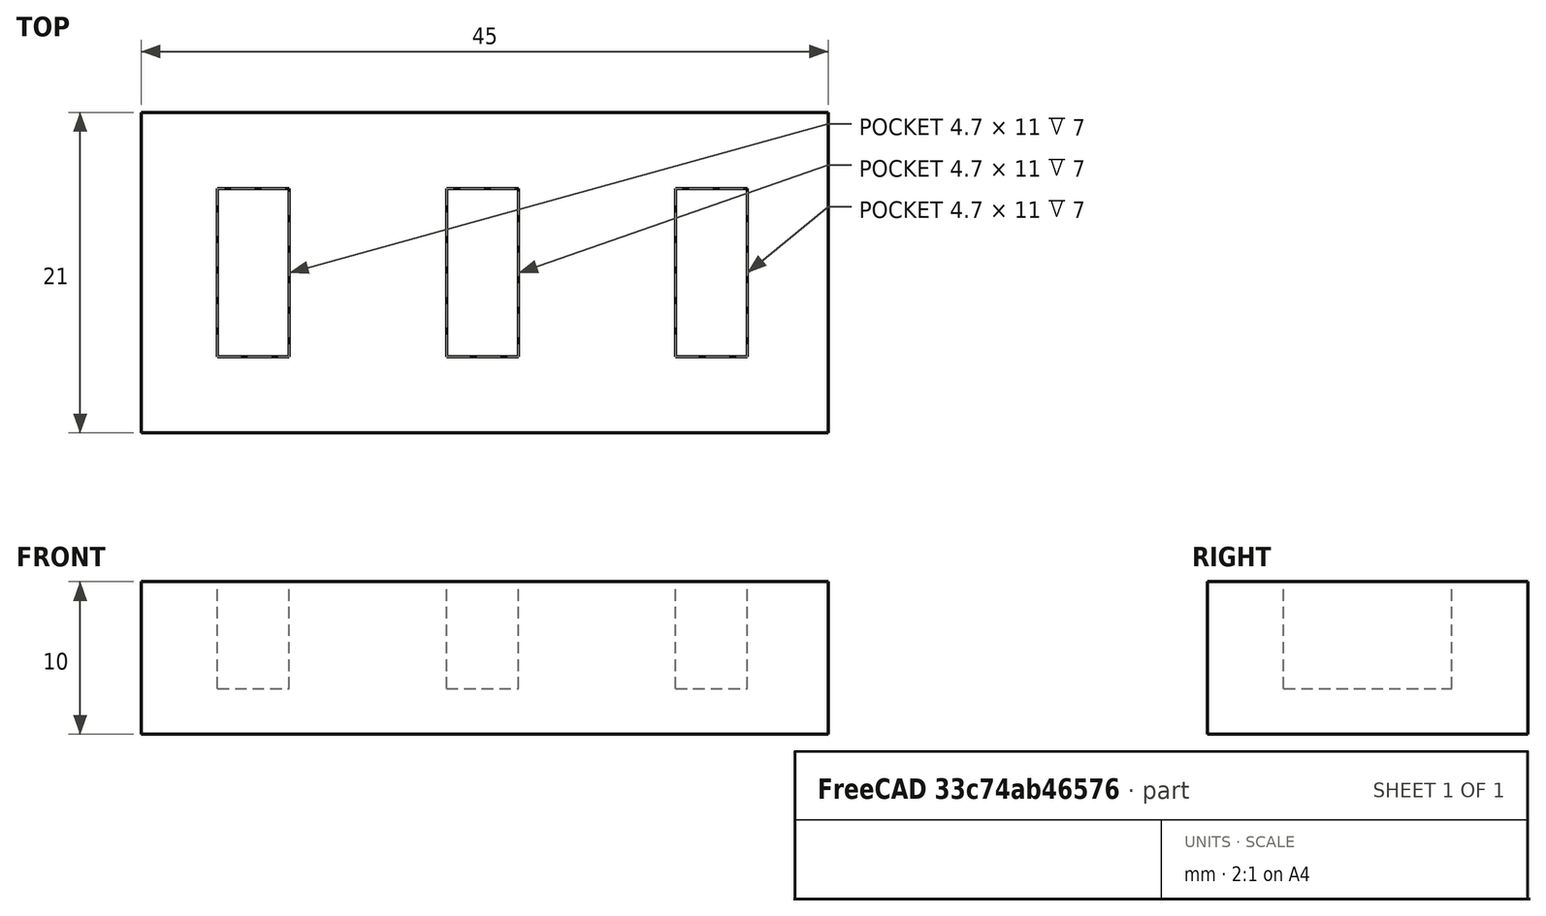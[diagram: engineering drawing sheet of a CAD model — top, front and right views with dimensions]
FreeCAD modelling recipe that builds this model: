
FCSTD DOCUMENT  (FreeCAD 1.0R39319 (Git))
Label: ojt1_t08p01_usb_flash
License: All rights reserved
LicenseURL: https://en.wikipedia.org/wiki/All_rights_reserved
objects: Part::Box×4, Part::MultiFuse×1, Part::Cut×1
note: 6 computed .brp shape members not serialized (recipe doc carries the construction recipe); baked Part::Feature solids carry a one-line shape summary decoded from their .brp

FEATURE [Part::Box] Box  label="ranura 1"
  AttacherType = Attacher::AttachEngine3D
  Height = 12
  Length = 4.7
  Width = 11
FEATURE [Part::Box] Box001  label="ranura 002"
  AttacherType = Attacher::AttachEngine3D
  Height = 12
  Length = 4.7
  Placement = pos=(15,0,0) rot=(0,0,1;0rad)
  Width = 11
FEATURE [Part::Box] Box002  label="ranura 003"
  AttacherType = Attacher::AttachEngine3D
  Height = 12
  Length = 4.7
  Placement = pos=(30,0,0) rot=(0,0,1;0rad)
  Width = 11
FEATURE [Part::MultiFuse] Fusion  label="ranuras"
  Placement = pos=(5,5,3) rot=(0,0,1;0rad)
  Refine = true
  Shapes = -> [Box,Box001,Box002]
FEATURE [Part::Box] Box003  label="base"
  AttacherType = Attacher::AttachEngine3D
  Height = 10
  Length = 45
  Width = 21
FEATURE [Part::Cut] Cut  label="porta-pendrives"
  Base = -> Box003
  Refine = true
  Tool = -> Fusion
